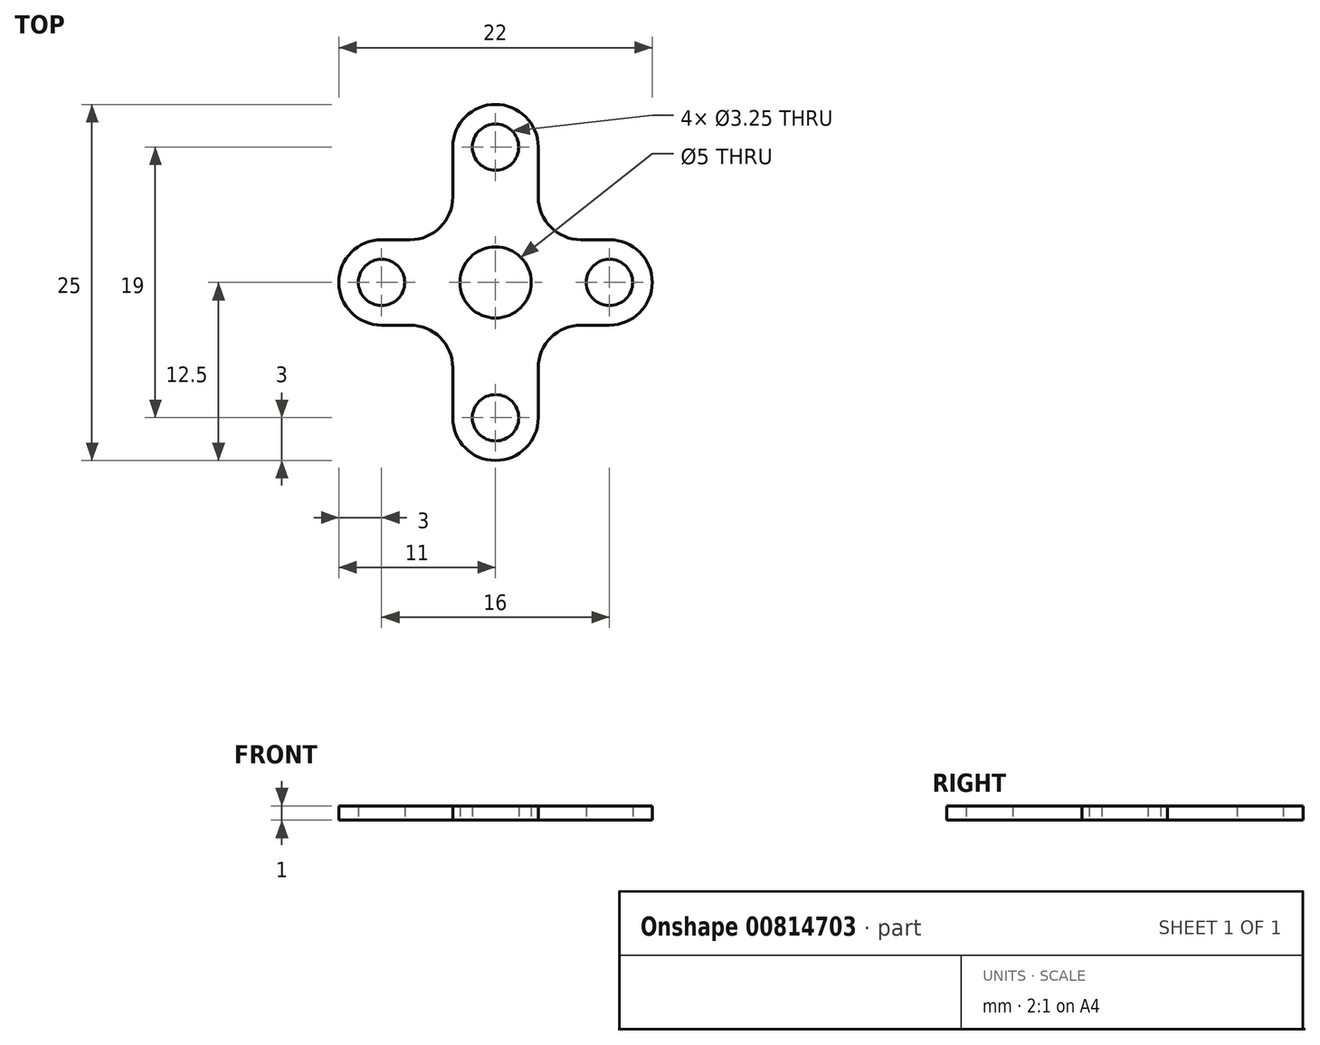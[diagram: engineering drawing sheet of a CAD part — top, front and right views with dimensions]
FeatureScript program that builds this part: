
annotation { "Feature Type Name" : "Feature", "Feature Type Description" : "" }
export const myFeature = defineFeature(function(context is Context, id is Id, definition is map)
    precondition{}
    {
        {
            var Q0;
            Q0=qCreatedBy(makeId("Top.planeOp"),FACE);
            var sketch = newSketch(context, id + "F0", { "sketchPlane" : qUnion([Q0])});
            skLineSegment(sketch, "E0", {"start": v(0, 0) * mm, "end": v(8, 0) * mm, "construction": true});
            skCircle(sketch, "E1", {"center": v(8, 0) * mm, "radius": 1.63 * mm});
            skLineSegment(sketch, "E2", {"start": v(0, 0) * mm, "end": v(0, -9.5) * mm, "construction": true});
            skCircle(sketch, "E3", {"center": v(0, -9.5) * mm, "radius": 1.63 * mm});
            skLineSegment(sketch, "E4", {"start": v(0, 0) * mm, "end": v(3, 3) * mm, "construction": true});
            skCircle(sketch, "E5.MirrorC", {"center": v(-8, 0) * mm, "radius": 1.63 * mm});
            skCircle(sketch, "E6.MirrorC", {"center": v(0, 9.5) * mm, "radius": 1.63 * mm});
            skArc(sketch, "E7", {"start": v(-3, 9.5) * mm, "mid": v(0, 12.5) * mm, "end": v(3, 9.5) * mm});
            skLineSegment(sketch, "E8", {"start": v(3, 9.5) * mm, "end": v(3, 6) * mm});
            skLineSegment(sketch, "E9", {"start": v(8, 3) * mm, "end": v(6, 3) * mm});
            skArc(sketch, "E10", {"start": v(8, 3) * mm, "mid": v(11, 0) * mm, "end": v(8, -3) * mm});
            skCircle(sketch, "E11", {"center": v(0, 0) * mm, "radius": 2.5 * mm});
            skLineSegment(sketch, "E12.MirrorCS", {"start": v(-3, 9.5) * mm, "end": v(-3, 6) * mm});
            skLineSegment(sketch, "E13.MirrorCS", {"start": v(-8, 3) * mm, "end": v(-6, 3) * mm});
            skArc(sketch, "E14.MirrorCS", {"start": v(-8, 3) * mm, "mid": v(-11, 0) * mm, "end": v(-8, -3) * mm});
            skArc(sketch, "E15.MirrorCS", {"start": v(-3, -9.5) * mm, "mid": v(0, -12.5) * mm, "end": v(3, -9.5) * mm});
            skLineSegment(sketch, "E16.MirrorCS", {"start": v(-3, -9.5) * mm, "end": v(-3, -6) * mm});
            skLineSegment(sketch, "E17.MirrorCS", {"start": v(3, -9.5) * mm, "end": v(3, -6) * mm});
            skLineSegment(sketch, "E18.MirrorCS", {"start": v(8, -3) * mm, "end": v(6, -3) * mm});
            skLineSegment(sketch, "E19.MirrorCS", {"start": v(-8, -3) * mm, "end": v(-6, -3) * mm});
            skPoint(sketch, "E20.visualSharp", {"position": v(3, 3) * mm});
            skArc(sketch, "E20.filletArc", {"start": v(3, 6) * mm, "mid": v(3.88, 3.88) * mm, "end": v(6, 3) * mm});
            skPoint(sketch, "E21.visualSharp", {"position": v(3, -3) * mm});
            skArc(sketch, "E21.filletArc", {"start": v(6, -3) * mm, "mid": v(3.88, -3.88) * mm, "end": v(3, -6) * mm});
            skPoint(sketch, "E22.visualSharp", {"position": v(-3, -3) * mm});
            skArc(sketch, "E22.filletArc", {"start": v(-3, -6) * mm, "mid": v(-3.88, -3.88) * mm, "end": v(-6, -3) * mm});
            skPoint(sketch, "E23.visualSharp", {"position": v(-3, 3) * mm});
            skArc(sketch, "E23.filletArc", {"start": v(-6, 3) * mm, "mid": v(-3.88, 3.88) * mm, "end": v(-3, 6) * mm});
            skSolve(sketch);
        }
        {
            var Q0;
            Q0 = qSketchRegion(id + "F0", true);
            extrude(context, id + "F1", {"entities" : qUnion([Q0]), "depth" : 1 * mm, "offsetDistance" : 25 * mm});
        }
    });
